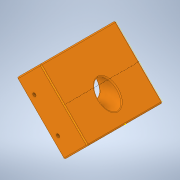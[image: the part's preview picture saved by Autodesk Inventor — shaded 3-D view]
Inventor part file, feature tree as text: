
AUTODESK INVENTOR PART (.ipt)
format: ipt  version: 2020.1 (Build 241239000, 239)  size: 250,880 bytes
history: native  units: in
note: dims shown in document units (in); Inventor stores cm internally (conversion verified against a paired STEP export)
features: fillet x6, sketch x5, extrude x3, plane x1, hole x1
ambient origin geometry x8: Origin, YZ Plane, XZ Plane, XY Plane, X Axis, Y Axis, Z Axis, Center Point
bodies: Solid1 (feature_tree)
feature tree (16):
  extrude  "Extrusion1"  TaperAngle=45.0deg  [1 undecoded]
  sketch  "Sketch3"  dims[d4=1.0in d5=45.0deg]
  plane  "Work Plane1"
  extrude  "Extrusion2"  TaperAngle=45.0deg  [1 undecoded]
  extrude  "Extrusion3"  TaperAngle=90.0deg  [1 undecoded]
  hole  "Hole2"  [1 undecoded]
  fillet  "Fillet1"  [1 undecoded]
  fillet  "Fillet2"  Radius=1.0in
  fillet  "Fillet3"  Radius=1.0in
  fillet  "Fillet4"  Radius=0.0625in
  fillet  "Fillet5"  Radius=0.0625in
  fillet  "Fillet6"  Radius=0.0625in
  sketch  "Sketch1"  dims[d1=135.0deg d3=45.0deg]
  sketch  "Sketch4"  dims[d7=0.0in d8=90.0deg]
  sketch  "Sketch5"  dims[d18=1.0in d19=0.0in d21=1.0in d24=0.0in d26=1.0in d27=1.0in]
  sketch  "Sketch6"  dims[d28=0.201in d29=0.75in d30=0.385in d31=0.25in d32=0.5635in d33=1.0in d34=0.8108in d35=0.0625in d36=0.0625in d37=0.0625in d38=0.0625in d39=0.0625in d40=0.0625in]
note: 5 required parameter values undecoded (feature->parameter linkage not recoverable at this tier; creation-order binding heuristic only, values carry confidence <= 0.55)
